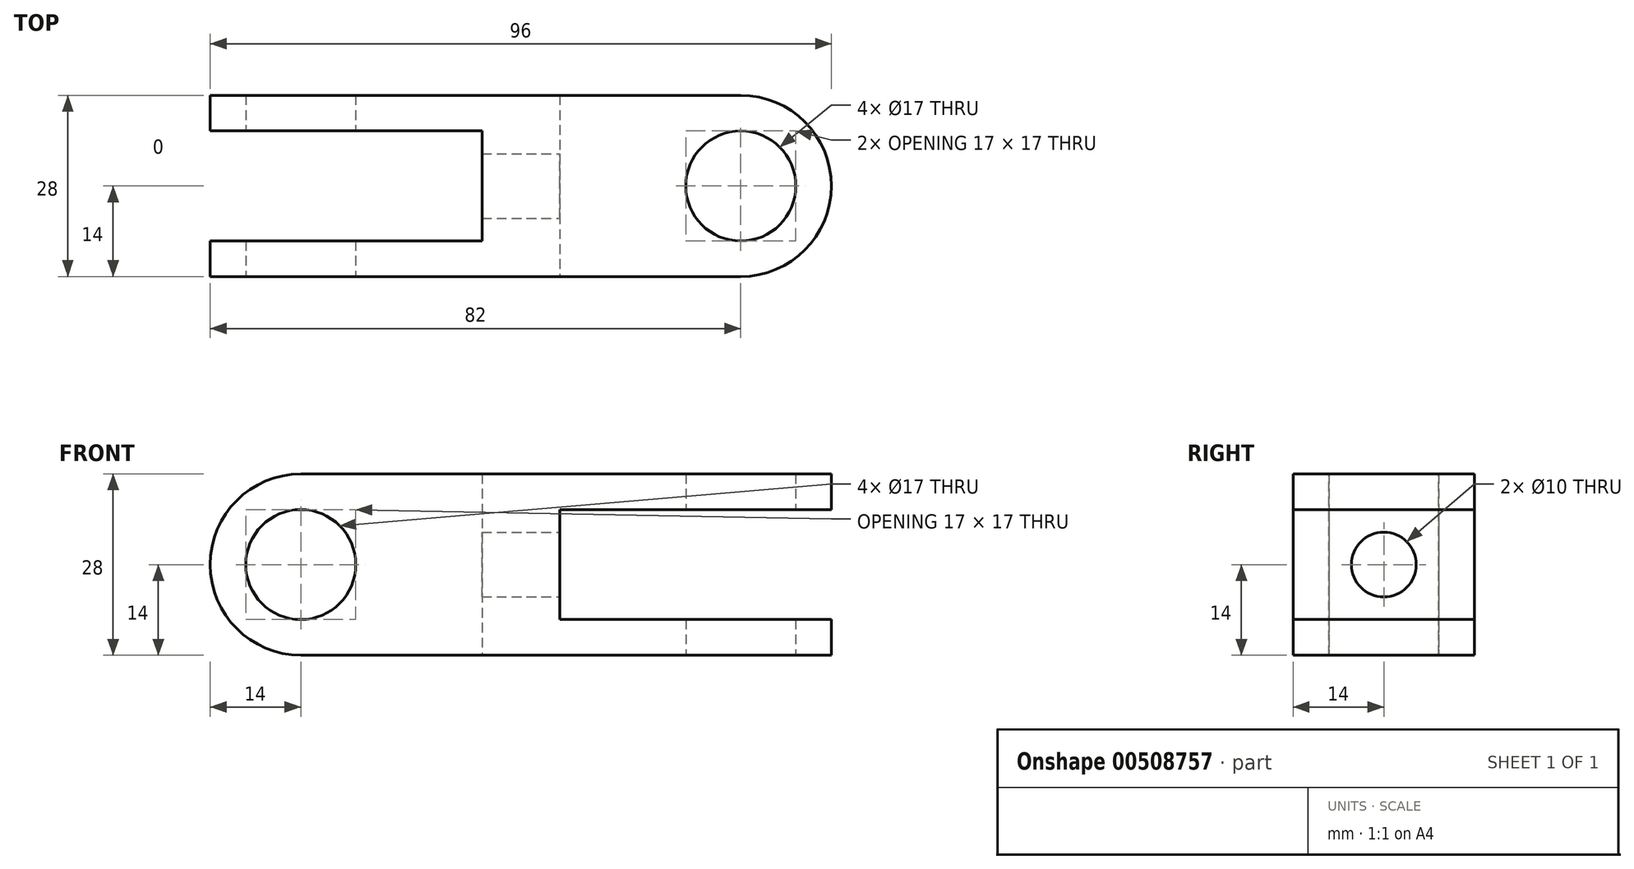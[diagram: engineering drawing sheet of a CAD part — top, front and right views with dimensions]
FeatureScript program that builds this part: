
annotation { "Feature Type Name" : "Feature", "Feature Type Description" : "" }
export const myFeature = defineFeature(function(context is Context, id is Id, definition is map)
    precondition{}
    {
        {
            var Q0;
            Q0=qCreatedBy(makeId("Top.planeOp"),FACE);
            var sketch = newSketch(context, id + "F0", { "sketchPlane" : qUnion([Q0])});
            skLineSegment(sketch, "E0.bottom", {"start": v(-41, 14) * mm, "end": v(41, 14) * mm});
            skLineSegment(sketch, "E0.top", {"start": v(-41, -14) * mm, "end": v(41, -14) * mm});
            skLineSegment(sketch, "E0.left", {"start": v(-41, 14) * mm, "end": v(-41, 8.5) * mm});
            skPoint(sketch, "E0.middle", {"position": v(0, 0) * mm});
            skArc(sketch, "E1", {"start": v(41, -14) * mm, "mid": v(55, 0) * mm, "end": v(41, 14) * mm});
            skCircle(sketch, "E2", {"center": v(41, 0) * mm, "radius": 8.5 * mm});
            skLineSegment(sketch, "E3.bottom", {"start": v(-41, 8.5) * mm, "end": v(1, 8.5) * mm});
            skLineSegment(sketch, "E3.top", {"start": v(-41, -8.5) * mm, "end": v(1, -8.5) * mm});
            skLineSegment(sketch, "E3.right", {"start": v(1, 8.5) * mm, "end": v(1, -8.5) * mm});
            skPoint(sketch, "E3.middle", {"position": v(-41, 0) * mm});
            skPoint(sketch, "E3.left.start.orphan", {"position": v(-83, 8.5) * mm});
            skPoint(sketch, "E4.orphan", {"position": v(-83, -8.5) * mm});
            skLineSegment(sketch, "E5.trimOffspring", {"start": v(-41, -8.5) * mm, "end": v(-41, -14) * mm});
            skSolve(sketch);
        }
        {
            var Q0;
            Q0 = qSketchRegion(id + "F0", true);
            extrude(context, id + "F1", {"entities" : qUnion([Q0]), "depth" : 28 * mm});
        }
        {
            var Q0;
            Q0=makeQuery(id+"F1.opExtrude","SWEPT_FACE",FACE,{"disambiguationData":[OSD([sQuery(id+"F0.wireOp",EDGE,"E0.top")])]});
            var sketch = newSketch(context, id + "F2", { "sketchPlane" : qUnion([Q0])});
            skCircle(sketch, "E6", {"center": v(-27, 14) * mm, "radius": 8.5 * mm});
            skPoint(sketch, "E6.centerSnap0", {"position": v(-41, 14) * mm});
            skLineSegment(sketch, "E7.bottom", {"start": v(13.03, 22.5) * mm, "end": v(97.03, 22.5) * mm});
            skLineSegment(sketch, "E7.top", {"start": v(13.03, 5.5) * mm, "end": v(97.03, 5.5) * mm});
            skLineSegment(sketch, "E7.left", {"start": v(13.03, 22.5) * mm, "end": v(13.03, 5.5) * mm});
            skLineSegment(sketch, "E7.right", {"start": v(97.03, 22.5) * mm, "end": v(97.03, 5.5) * mm});
            skPoint(sketch, "E7.middle", {"position": v(55.03, 14) * mm});
            skPoint(sketch, "E7.middle.positionSnap0", {"position": v(41, 14) * mm});
            skPoint(sketch, "E7.centerSnap0", {"position": v(41, 14) * mm});
            skSolve(sketch);
        }
        {
            var Q0;
            Q0 = qSketchRegion(id + "F2", true);
            extrude(context, id + "F3", {"entities" : qUnion([Q0]), "operationType" : NewBodyOperationType.REMOVE, "endBound" : BoundingType.THROUGH_ALL, "oppositeDirection" : true, "depth" : 25 * mm});
        }
        {
            var Q0;
            Q0=makeQuery(id+"F1.opExtrude","CAP_EDGE",EDGE,{"disambiguationData":[OSD([sQuery(id+"F0.wireOp",EDGE,"E0.left")])],"isStart":false});
            var Q1;
            Q1=makeQuery(id+"F1.opExtrude","CAP_EDGE",EDGE,{"disambiguationData":[OSD([sQuery(id+"F0.wireOp",EDGE,"E0.left")])],"isStart":true});
            var Q2;
            Q2=makeQuery(id+"F1.opExtrude","CAP_EDGE",EDGE,{"disambiguationData":[OSD([sQuery(id+"F0.wireOp",EDGE,"E5.trimOffspring")])],"isStart":false});
            var Q3;
            Q3=makeQuery(id+"F1.opExtrude","CAP_EDGE",EDGE,{"disambiguationData":[OSD([sQuery(id+"F0.wireOp",EDGE,"E5.trimOffspring")])],"isStart":true});
            fillet(context, id + "F4", {"entities" : qUnion([Q0, Q1, Q2, Q3]), "radius" : 14 * mm, "tangentPropagation" : true, "allowEdgeOverflow" : false});
        }
        {
            var Q0;
            Q0=makeQuery(id+"F3.boolean.opBoolean","COPY",FACE,{"derivedFrom":makeQuery(id+"F3.opExtrude","SWEPT_FACE",FACE,{"disambiguationData":[OSD([sQuery(id+"F2.wireOp",EDGE,"E7.left")])]})});
            var sketch = newSketch(context, id + "F5", { "sketchPlane" : qUnion([Q0])});
            skCircle(sketch, "E8", {"center": v(0, 14) * mm, "radius": 5 * mm});
            skPoint(sketch, "E8.centerSnap0", {"position": v(-14, 14) * mm});
            skSolve(sketch);
        }
        {
            var Q0;
            Q0 = qSketchRegion(id + "F5", true);
            extrude(context, id + "F6", {"entities" : qUnion([Q0]), "operationType" : NewBodyOperationType.REMOVE, "endBound" : BoundingType.THROUGH_ALL, "oppositeDirection" : true, "depth" : 25 * mm});
        }
    });
